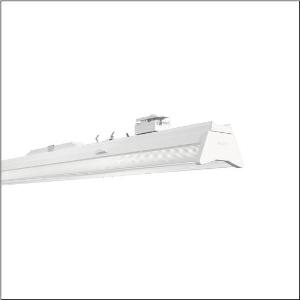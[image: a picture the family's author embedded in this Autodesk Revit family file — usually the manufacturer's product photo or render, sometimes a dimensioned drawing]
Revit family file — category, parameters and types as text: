
# Revit family: licross_r__11_performance_mo_51tm16dn4axg_9905
name_source: partatom
category: Lighting Fixtures
units: mm (PartAtom-declared; Revit-internal decimal feet)

## family parameters
Cut with Voids When Loaded = No
Host = Face
Light Source = No
Part Type = Normal
Room Calculation Point = No
Round Connector Dimension = Use Diameter
Shared = No

## types (1)
- --- (1 x LED, 10110 lm, 57.1 W, 4000K)
    Apparent Load = 57 VA
    CIE Flux Codes = 66 88 96 79 100
    Color Rendering = 80
    Color Temperature = 4000K
    Default Elevation = 1800 mm
    Description = Licross® 11 Performance MO, luminaire insert, of sheet steel, galvanised, coil coated, white, length: 1.500mm, width: 120mm, height: 123mm, LED rated luminous flux: 10.110lm, light colour: 840, control gear: DALI 2, with plug, 5-pole, with phase selection, mains connection: 220..240V, AC, 50/60Hz, rated input power: 57W, halogen-free wiring, primary light control with lens, of plastic, primary optical cover: cover, of PMMA, light emission: direct/indirect distribution, primary light characteristic: symmetric, protection rating (complete): IP40, insulation class (complete): insulation class I (protective earthing), certification: CE, ENEC, VDE, UKCA, protection symbol: D if used in an environment without relevant dust loads with corresponding accessories, impact resistance: IK06, permissible ambient temperature for indoor applications: -25..+35°C, corresponds to IFS (International Featured Standards) requirements for safety and quality in the food industry, reducing of maximum allowable ambient temperature of 5°C with ceiling mounting, LABS conformity tested according to VDMA 24364:2018-05, packaging unit: 1 piece
    Height = 114 mm
    Lamp = 1 x LED
    Lamp Light Flux = 10110 lm
    Lamp Power = 57.1 W
    Lamp count = 1
    Length = 1500 mm
    Luminous efficacy = 177 lm/W
    Manufacturer = Siteco
    ModVariant = No
    Model = 51TM16DN4AXG
    Mounting Place = Ceiling
    Mounting Type = Pendant
    Number of Poles = 1
    OnlyDefault = Yes
    Power Factor = 1
    Product Name = Licross® 11 Performance MO
    Product group = luminaire insert
    ProductGroupID = 901
    Protection Class = Protection class I
    Protection Degree = IP 40
    RLX_Detail_Level = 1
    RLX_Emergency_Light_Flux = 0 lm
    RLX_Emergency_Type = 0
    RLX_Emergency_Type_DB = No
    RlxData = <blob elided: 34061 chars, md5=06fa0c3e>
    Socket = socket
    Standby Power = 0 W
    System Light Flux = 10110 lm
    System Power = 57 W
    Type Comments = factory setting: luminous flux: 100 % | dim-lin: 254 | 378 mA
    Type Image = l_1256138.jpg
    URL = http://relux.com
    VarID = @adj_070197
    Voltage = 0 V
    Weight = 0.00 kg
    Width = 120 mm

## geometry (parser evidence)
native form markers: Blend x4, Sweep x13
no freeform markers — native parametric forms only
